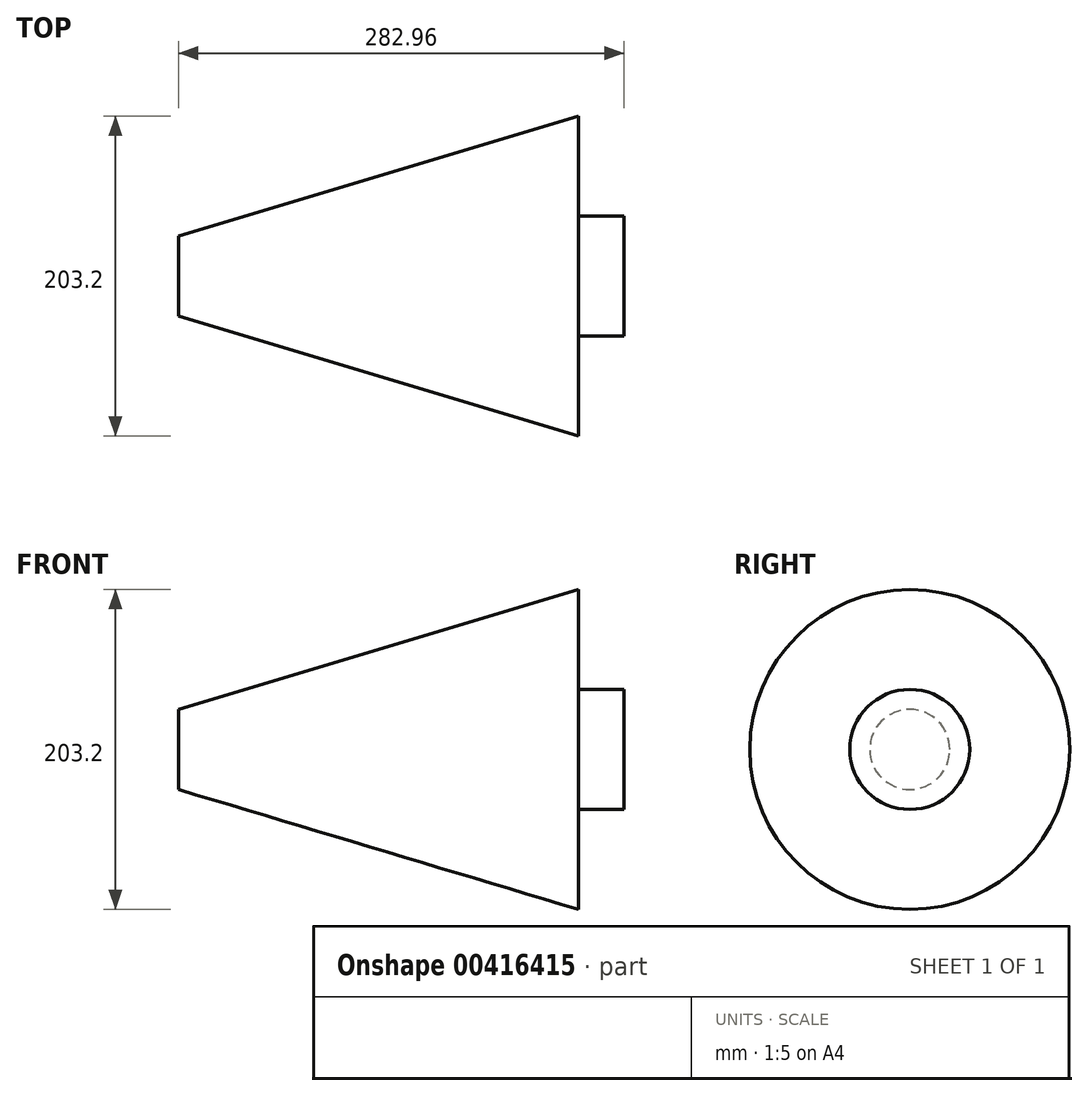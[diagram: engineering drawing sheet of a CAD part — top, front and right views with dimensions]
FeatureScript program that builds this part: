
annotation { "Feature Type Name" : "Feature", "Feature Type Description" : "" }
export const myFeature = defineFeature(function(context is Context, id is Id, definition is map)
    precondition{}
    {
        {
            var Q0;
            Q0=qCreatedBy(makeId("Right.planeOp"),FACE);
            var sketch = newSketch(context, id + "F0", { "sketchPlane" : qUnion([Q0])});
            skCircle(sketch, "E0", {"center": v(0, 0) * mm, "radius": 101.6 * mm});
            skSolve(sketch);
        }
        {
            var Q0;
            Q0=qCreatedBy(makeId("Top.planeOp"),FACE);
            var sketch = newSketch(context, id + "F1", { "sketchPlane" : qUnion([Q0])});
            skLineSegment(sketch, "E1", {"start": v(0, 0) * mm, "end": v(-254, 0) * mm});
            skLineSegment(sketch, "E2", {"start": v(0, 0) * mm, "end": v(0, -101.6) * mm});
            skLineSegment(sketch, "E3", {"start": v(-254, 0) * mm, "end": v(-254, -25.4) * mm});
            skLineSegment(sketch, "E4", {"start": v(-254, -25.4) * mm, "end": v(0, -101.6) * mm});
            skSolve(sketch);
        }
        {
            var Q0;
            Q0=makeQuery(id+"F1.imprint","IMPRINT",FACE,{"disambiguationData":[TD([[makeQuery(id+"F1.imprint","IMPRINT",EDGE,{"derivedFrom":sQuery(id+"F1.wireOp",EDGE,"E1")}),1.0]])]});
            var Q1;
            Q1=sQuery(id+"F1.wireOp",EDGE,"E1");
            revolve(context, id + "F2", {"entities" : qUnion([Q0]), "axis" : qUnion([Q1]), "revolveType" : RevolveType.FULL});
        }
        {
            var Q0;
            Q0=makeQuery(id+"F0.imprint","IMPRINT",FACE,{"disambiguationData":[TD([[makeQuery(id+"F0.imprint","IMPRINT",EDGE,{"derivedFrom":sQuery(id+"F0.wireOp",EDGE,"E0")}),1.0]])]});
            var sketch = newSketch(context, id + "F3", { "sketchPlane" : qUnion([Q0])});
            skCircle(sketch, "E5", {"center": v(0, 0) * mm, "radius": 38.1 * mm});
            skSolve(sketch);
        }
        {
            var Q0;
            Q0=makeQuery(id+"F3.imprint","IMPRINT",FACE,{"disambiguationData":[TD([[makeQuery(id+"F3.imprint","IMPRINT",EDGE,{"derivedFrom":sQuery(id+"F3.wireOp",EDGE,"E5")}),1.0]])]});
            extrude(context, id + "F4", {"entities" : qUnion([Q0]), "operationType" : NewBodyOperationType.ADD, "depth" : 28.96 * mm});
        }
    });
